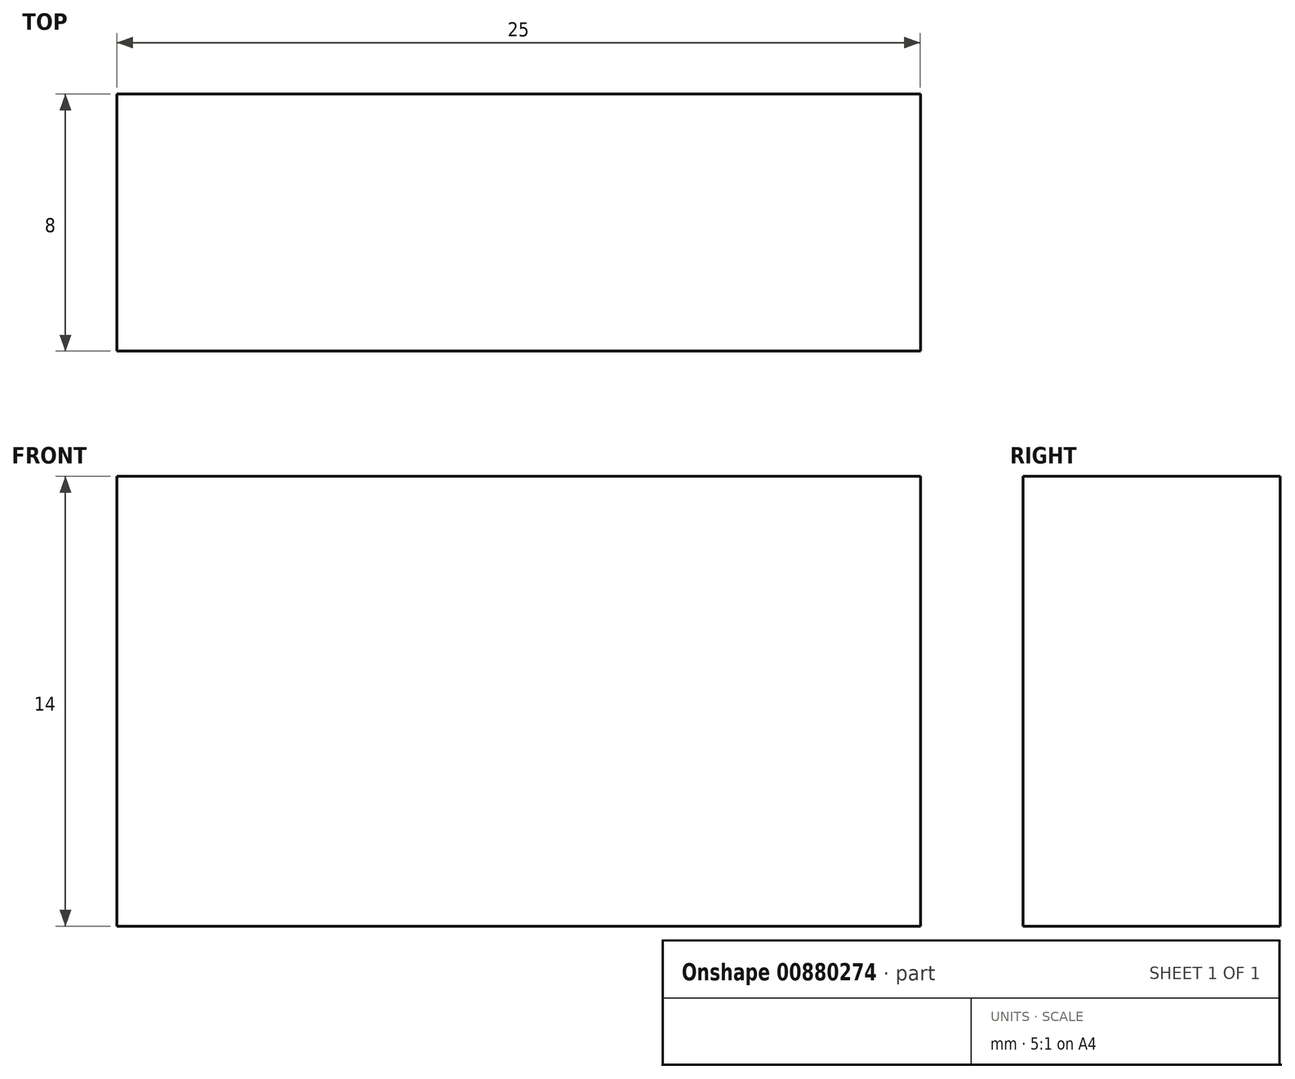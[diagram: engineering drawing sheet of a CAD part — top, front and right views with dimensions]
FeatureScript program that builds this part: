
annotation { "Feature Type Name" : "Feature", "Feature Type Description" : "" }
export const myFeature = defineFeature(function(context is Context, id is Id, definition is map)
    precondition{}
    {
        {
            var Q0;
            Q0=qCreatedBy(makeId("Front.planeOp"),FACE);
            var sketch = newSketch(context, id + "F0", { "sketchPlane" : qUnion([Q0])});
            skLineSegment(sketch, "E0.bottom", {"start": v(-66.04, 59.08) * mm, "end": v(-41.04, 59.08) * mm});
            skLineSegment(sketch, "E0.top", {"start": v(-66.04, 45.08) * mm, "end": v(-41.04, 45.08) * mm});
            skLineSegment(sketch, "E0.left", {"start": v(-66.04, 59.08) * mm, "end": v(-66.04, 45.08) * mm});
            skLineSegment(sketch, "E0.right", {"start": v(-41.04, 59.08) * mm, "end": v(-41.04, 45.08) * mm});
            skSolve(sketch);
        }
        {
            var Q0;
            Q0=makeQuery(id+"F0.imprint","IMPRINT",FACE,{"disambiguationData":[TD([[makeQuery(id+"F0.imprint","IMPRINT",EDGE,{"derivedFrom":sQuery(id+"F0.wireOp",EDGE,"E0.bottom")}),-1.0]])]});
            extrude(context, id + "F1", {"entities" : qUnion([Q0]), "depth" : 8 * mm, "offsetDistance" : 25 * mm});
        }
    });
